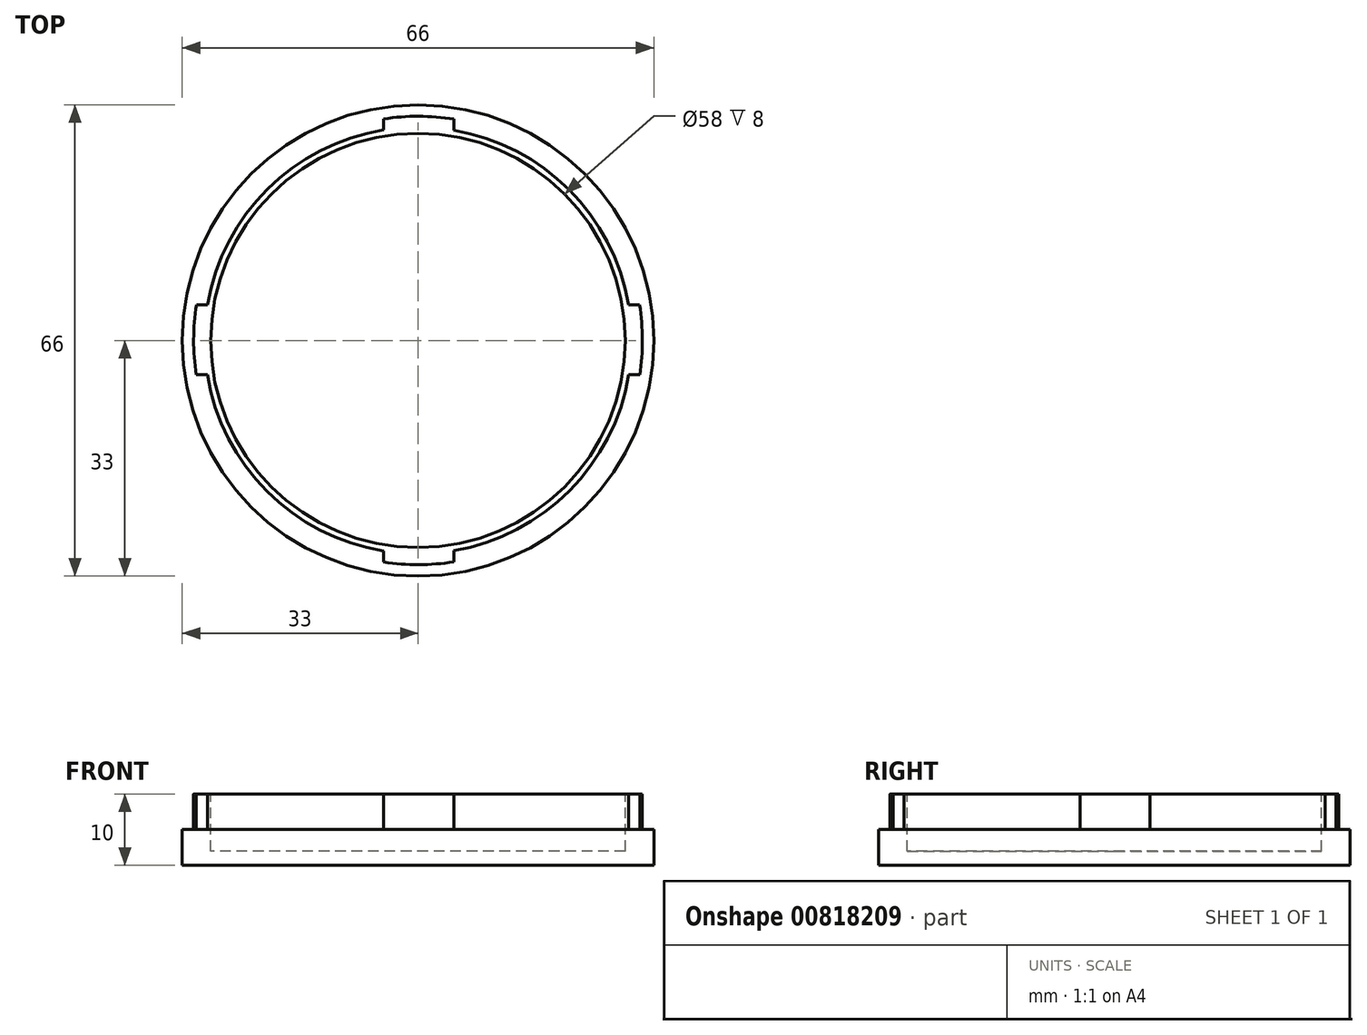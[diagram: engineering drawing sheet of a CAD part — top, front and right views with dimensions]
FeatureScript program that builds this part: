
annotation { "Feature Type Name" : "Feature", "Feature Type Description" : "" }
export const myFeature = defineFeature(function(context is Context, id is Id, definition is map)
    precondition{}
    {
        {
            var Q0;
            Q0=qCreatedBy(makeId("Front.planeOp"),FACE);
            var sketch = newSketch(context, id + "F0", { "sketchPlane" : qUnion([Q0])});
            skLineSegment(sketch, "E0", {"start": v(31.4, -16.49) * mm, "end": v(31.4, -21.49) * mm});
            skLineSegment(sketch, "E1", {"start": v(33, -21.49) * mm, "end": v(33, -26.49) * mm});
            skLineSegment(sketch, "E2", {"start": v(33, -26.49) * mm, "end": v(0, -26.49) * mm});
            skLineSegment(sketch, "E3", {"start": v(31.4, -16.49) * mm, "end": v(29, -16.49) * mm});
            skLineSegment(sketch, "E4", {"start": v(29, -16.49) * mm, "end": v(29, -24.49) * mm});
            skLineSegment(sketch, "E5", {"start": v(29, -24.49) * mm, "end": v(0, -24.49) * mm});
            skLineSegment(sketch, "E6", {"start": v(0, -24.49) * mm, "end": v(0, -26.49) * mm});
            skLineSegment(sketch, "E7", {"start": v(31.4, -21.49) * mm, "end": v(33, -21.49) * mm});
            skSolve(sketch);
        }
        {
            var Q0;
            Q0 = qSketchRegion(id + "F0", true);
            var Q1;
            Q1=sQuery(id+"F0.wireOp",EDGE,"E6");
            revolve(context, id + "F1", {"surfaceOperationType" : NewSurfaceOperationType.NEW, "entities" : qUnion([Q0]), "axis" : qUnion([Q1]), "revolveType" : RevolveType.FULL});
        }
        {
            var Q0;
            Q0=makeQuery(id+"F1.opRevolve","SWEPT_FACE",FACE,{"disambiguationData":[OSD([sQuery(id+"F0.wireOp",EDGE,"E3")])]});
            var sketch = newSketch(context, id + "F2", { "sketchPlane" : qUnion([Q0])});
            skLineSegment(sketch, "E8.left", {"start": v(-41.48, 5) * mm, "end": v(-41.48, -4.8) * mm, "construction": true});
            skLineSegment(sketch, "E8.right", {"start": v(50.33, 5) * mm, "end": v(50.33, -4.8) * mm, "construction": true});
            skLineSegment(sketch, "E9.bottom", {"start": v(-4.8, 34.28) * mm, "end": v(5, 34.28) * mm, "construction": true});
            skLineSegment(sketch, "E9.top", {"start": v(-4.8, -38.96) * mm, "end": v(5, -38.96) * mm, "construction": true});
            skCircle(sketch, "E10", {"center": v(0, 0) * mm, "radius": 29.9 * mm, "construction": true});
            skPoint(sketch, "E11", {"position": v(-31, 5) * mm});
            skPoint(sketch, "E12", {"position": v(-4.8, 29.51) * mm});
            skPoint(sketch, "E13", {"position": v(-4.8, 28.6) * mm});
            skPoint(sketch, "E14", {"position": v(5, 28.57) * mm});
            skPoint(sketch, "E15", {"position": v(5, 29.51) * mm});
            skPoint(sketch, "E16", {"position": v(-29.48, 5) * mm});
            skPoint(sketch, "E17", {"position": v(-29.51, -4.8) * mm});
            skPoint(sketch, "E18", {"position": v(-28.6, -4.8) * mm});
            skPoint(sketch, "E19", {"position": v(-28.57, 5) * mm});
            skPoint(sketch, "E20", {"position": v(-4.8, -28.6) * mm});
            skPoint(sketch, "E21", {"position": v(-4.8, -29.51) * mm});
            skPoint(sketch, "E22", {"position": v(5, -29.48) * mm});
            skPoint(sketch, "E23", {"position": v(5, -28.57) * mm});
            skPoint(sketch, "E24", {"position": v(28.57, 5) * mm});
            skPoint(sketch, "E25", {"position": v(29.48, 5) * mm});
            skPoint(sketch, "E26", {"position": v(29.51, -4.8) * mm});
            skPoint(sketch, "E27", {"position": v(28.6, -4.8) * mm});
            skCircle(sketch, "E28", {"center": v(0, 0) * mm, "radius": 29.87 * mm});
            skLineSegment(sketch, "E29", {"start": v(-29.48, 5) * mm, "end": v(28.57, 5) * mm});
            skLineSegment(sketch, "E30", {"start": v(-4.8, 29.51) * mm, "end": v(-4.8, -29.51) * mm});
            skLineSegment(sketch, "E31", {"start": v(5, -29.48) * mm, "end": v(5, 29.51) * mm});
            skLineSegment(sketch, "E32", {"start": v(-29.51, -4.8) * mm, "end": v(29.51, -4.8) * mm});
            skPoint(sketch, "E33", {"position": v(-4.8, 31.03) * mm});
            skPoint(sketch, "E34", {"position": v(5, 31) * mm});
            skPoint(sketch, "E35", {"position": v(31, 5) * mm});
            skPoint(sketch, "E36", {"position": v(31.03, -4.8) * mm});
            skPoint(sketch, "E37", {"position": v(5, -31) * mm});
            skPoint(sketch, "E38", {"position": v(-4.8, -31.03) * mm});
            skPoint(sketch, "E39", {"position": v(-31.03, -4.8) * mm});
            skLineSegment(sketch, "E40", {"start": v(-31, 5) * mm, "end": v(-29.48, 5) * mm});
            skLineSegment(sketch, "E41", {"start": v(-31.03, -4.8) * mm, "end": v(-29.51, -4.8) * mm});
            skLineSegment(sketch, "E42", {"start": v(-4.8, -31.03) * mm, "end": v(-4.8, -29.51) * mm});
            skLineSegment(sketch, "E43", {"start": v(5, -31) * mm, "end": v(5, -29.48) * mm});
            skLineSegment(sketch, "E44", {"start": v(31.03, -4.8) * mm, "end": v(29.51, -4.8) * mm});
            skLineSegment(sketch, "E45", {"start": v(31, 5) * mm, "end": v(29.48, 5) * mm});
            skLineSegment(sketch, "E46", {"start": v(-4.8, 31.03) * mm, "end": v(-4.8, 29.51) * mm});
            skLineSegment(sketch, "E47", {"start": v(5, 31) * mm, "end": v(5, 29.51) * mm});
            skLineSegment(sketch, "E48", {"start": v(28.57, 5) * mm, "end": v(29.48, 5) * mm});
            skSolve(sketch);
        }
        {
            var Q0;
            {var subQ0=sQuery(id+"F2.wireOp",EDGE,"E40");Q0=makeQuery(id+"F2.imprint","IMPRINT",FACE,{"disambiguationData":[TD([[makeQuery(id+"F2.imprint","IMPRINT",EDGE,{"derivedFrom":subQ0}),1.0]])]});}
            var Q1;
            {var subQ0=sQuery(id+"F2.wireOp",EDGE,"E41");Q1=makeQuery(id+"F2.imprint","IMPRINT",FACE,{"disambiguationData":[TD([[makeQuery(id+"F2.imprint","IMPRINT",EDGE,{"derivedFrom":subQ0}),-1.0]])]});}
            var Q2;
            {var subQ0=sQuery(id+"F2.wireOp",EDGE,"E43");Q2=makeQuery(id+"F2.imprint","IMPRINT",FACE,{"disambiguationData":[TD([[makeQuery(id+"F2.imprint","IMPRINT",EDGE,{"derivedFrom":subQ0}),-1.0]])]});}
            var Q3;
            {var subQ0=sQuery(id+"F2.wireOp",EDGE,"E45");Q3=makeQuery(id+"F2.imprint","IMPRINT",FACE,{"disambiguationData":[TD([[makeQuery(id+"F2.imprint","IMPRINT",EDGE,{"derivedFrom":subQ0}),-1.0]])]});}
            extrude(context, id + "F3", {"entities" : qUnion([Q0, Q1, Q2, Q3]), "operationType" : NewBodyOperationType.REMOVE, "oppositeDirection" : true, "depth" : 5 * mm, "offsetDistance" : 25 * mm});
        }
    });
